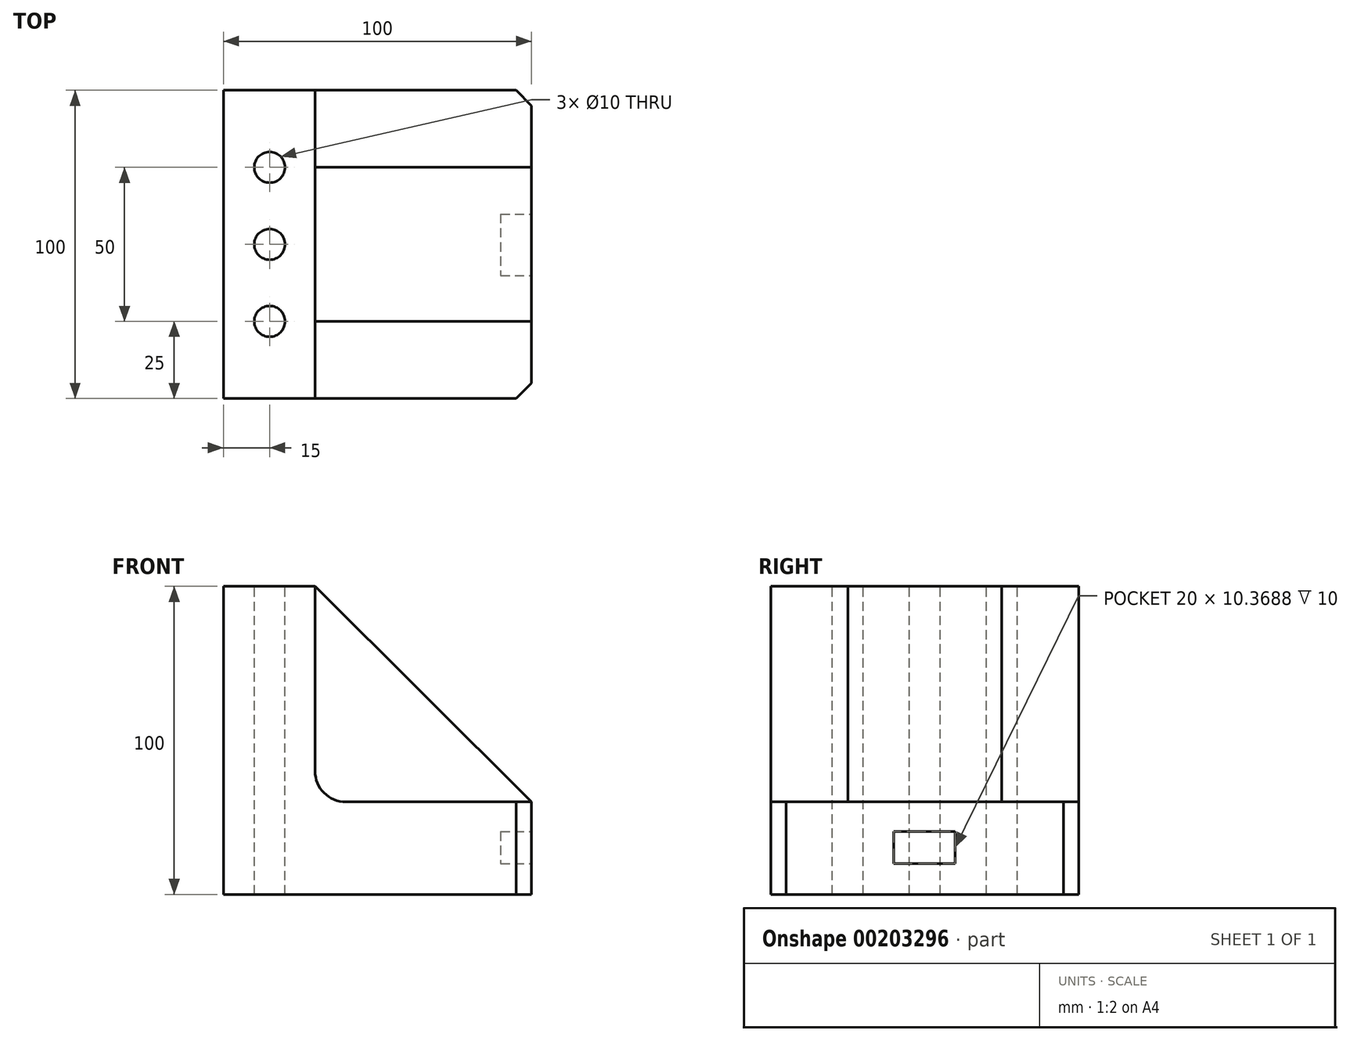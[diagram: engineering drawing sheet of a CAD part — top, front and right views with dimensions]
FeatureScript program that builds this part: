
annotation { "Feature Type Name" : "Feature", "Feature Type Description" : "" }
export const myFeature = defineFeature(function(context is Context, id is Id, definition is map)
    precondition{}
    {
        {
            var Q0;
            Q0=qCreatedBy(makeId("Top.planeOp"),FACE);
            var sketch = newSketch(context, id + "F0", { "sketchPlane" : qUnion([Q0])});
            skLineSegment(sketch, "E0.bottom", {"start": v(0, 0) * mm, "end": v(100, 0) * mm});
            skLineSegment(sketch, "E0.top", {"start": v(0, 100) * mm, "end": v(100, 100) * mm});
            skLineSegment(sketch, "E0.left", {"start": v(0, 0) * mm, "end": v(0, 100) * mm});
            skLineSegment(sketch, "E0.right", {"start": v(100, 0) * mm, "end": v(100, 100) * mm});
            skSolve(sketch);
        }
        {
            var Q0;
            Q0=makeQuery(id+"F0.imprint","IMPRINT",FACE,{"disambiguationData":[TD([[makeQuery(id+"F0.imprint","IMPRINT",EDGE,{"derivedFrom":sQuery(id+"F0.wireOp",EDGE,"E0.bottom")}),1.0]])]});
            extrude(context, id + "F1", {"entities" : qUnion([Q0]), "depth" : 100 * mm});
        }
        {
            var Q0;
            Q0=makeQuery(id+"F1.opExtrude","CAP_FACE",FACE,{"disambiguationData":[OSD([sQuery(id+"F0.wireOp",EDGE,"E0.bottom"),sQuery(id+"F0.wireOp",EDGE,"E0.top"),sQuery(id+"F0.wireOp",EDGE,"E0.left"),sQuery(id+"F0.wireOp",EDGE,"E0.right")])],"isStart":false});
            var sketch = newSketch(context, id + "F2", { "sketchPlane" : qUnion([Q0])});
            skLineSegment(sketch, "E1", {"start": v(0, 0) * mm, "end": v(30, 0) * mm});
            skLineSegment(sketch, "E2", {"start": v(30, 0) * mm, "end": v(30, 100) * mm});
            skCircle(sketch, "E3", {"center": v(15, 25) * mm, "radius": 5 * mm});
            skCircle(sketch, "E4", {"center": v(15, 50) * mm, "radius": 5 * mm});
            skCircle(sketch, "E5", {"center": v(15, 75) * mm, "radius": 5 * mm});
            skLineSegment(sketch, "E6", {"start": v(30, 0) * mm, "end": v(30, 25) * mm});
            skLineSegment(sketch, "E7", {"start": v(30, 100) * mm, "end": v(30, 75) * mm});
            skSolve(sketch);
        }
        {
            var Q0;
            Q0=makeQuery(id+"F2.imprint","IMPRINT",FACE,{"disambiguationData":[TD([[makeQuery(id+"F2.imprint","IMPRINT",EDGE,{"derivedFrom":sQuery(id+"F2.wireOp",EDGE,"E3")}),1.0]])]});
            var Q1;
            Q1=makeQuery(id+"F2.imprint","IMPRINT",FACE,{"disambiguationData":[TD([[makeQuery(id+"F2.imprint","IMPRINT",EDGE,{"derivedFrom":sQuery(id+"F2.wireOp",EDGE,"E4")}),1.0]])]});
            var Q2;
            Q2=makeQuery(id+"F2.imprint","IMPRINT",FACE,{"disambiguationData":[TD([[makeQuery(id+"F2.imprint","IMPRINT",EDGE,{"derivedFrom":sQuery(id+"F2.wireOp",EDGE,"E5")}),1.0]])]});
            extrude(context, id + "F3", {"entities" : qUnion([Q0, Q1, Q2]), "operationType" : NewBodyOperationType.REMOVE, "oppositeDirection" : true, "depth" : 100 * mm});
        }
        {
            var Q0;
            Q0=makeQuery(id+"F1.opExtrude","SWEPT_FACE",FACE,{"disambiguationData":[OSD([sQuery(id+"F0.wireOp",EDGE,"E0.bottom")])]});
            var sketch = newSketch(context, id + "F4", { "sketchPlane" : qUnion([Q0])});
            skLineSegment(sketch, "E8", {"start": v(50, 0) * mm, "end": v(50, 30) * mm});
            skPoint(sketch, "E9", {"position": v(29.74, 30) * mm});
            skLineSegment(sketch, "E10", {"start": v(29.74, 40) * mm, "end": v(29.74, 100) * mm});
            skArc(sketch, "E11.filletArc", {"start": v(29.74, 40) * mm, "mid": v(32.67, 32.93) * mm, "end": v(39.74, 30) * mm});
            skLineSegment(sketch, "E12", {"start": v(39.74, 30) * mm, "end": v(100, 30) * mm});
            skSolve(sketch);
        }
        {
            var Q0;
            Q0 = qSketchRegion(id + "F4", true);
            var Q1;
            {var subQ5=sQuery(id+"F4.wireOp",EDGE,"E10");Q1=makeQuery(id+"F4.imprint","IMPRINT",FACE,{"disambiguationData":[TD([[makeQuery(id+"F4.imprint","IMPRINT",EDGE,{"derivedFrom":subQ5}),-1.0]])]});}
            extrude(context, id + "F5", {"entities" : qUnion([Q0, Q1]), "operationType" : NewBodyOperationType.REMOVE, "oppositeDirection" : true, "depth" : 25 * mm});
        }
        {
            var Q0;
            Q0=makeQuery(id+"F1.opExtrude","SWEPT_FACE",FACE,{"disambiguationData":[OSD([sQuery(id+"F0.wireOp",EDGE,"E0.right")])]});
            var sketch = newSketch(context, id + "F6", { "sketchPlane" : qUnion([Q0])});
            skLineSegment(sketch, "E13", {"start": v(25, 30) * mm, "end": v(100, 30) * mm});
            skSolve(sketch);
        }
        {
            var Q0;
            Q0=makeQuery(id+"F1.opExtrude","SWEPT_FACE",FACE,{"disambiguationData":[OSD([sQuery(id+"F0.wireOp",EDGE,"E0.top")])]});
            var sketch = newSketch(context, id + "F7", { "sketchPlane" : qUnion([Q0])});
            skPoint(sketch, "E14", {"position": v(-29.74, 100) * mm});
            skPoint(sketch, "E15", {"position": v(-29.74, 30) * mm});
            skLineSegment(sketch, "E16", {"start": v(-39.74, 30) * mm, "end": v(-100, 30) * mm});
            skLineSegment(sketch, "E17", {"start": v(-29.74, 100) * mm, "end": v(-29.74, 40) * mm});
            skArc(sketch, "E18.filletArc", {"start": v(-39.74, 30) * mm, "mid": v(-32.67, 32.93) * mm, "end": v(-29.74, 40) * mm});
            skSolve(sketch);
        }
        {
            var Q0;
            {var subQ4=sQuery(id+"F7.wireOp",EDGE,"E16");Q0=makeQuery(id+"F7.imprint","IMPRINT",FACE,{"disambiguationData":[TD([[makeQuery(id+"F7.imprint","IMPRINT",EDGE,{"derivedFrom":subQ4}),-1.0]])]});}
            extrude(context, id + "F8", {"entities" : qUnion([Q0]), "operationType" : NewBodyOperationType.REMOVE, "oppositeDirection" : true, "depth" : 25 * mm});
        }
        {
            var Q0;
            Q0=makeQuery(id+"F5.boolean.opBoolean","COPY",FACE,{"derivedFrom":makeQuery(id+"F5.opExtrude","CAP_FACE",FACE,{"disambiguationData":[OSD([sQuery(id+"F0.wireOp",EDGE,"E0.bottom"),sQuery(id+"F0.wireOp",EDGE,"E0.right"),sQuery(id+"F4.wireOp",EDGE,"E10"),sQuery(id+"F4.wireOp",EDGE,"E11.filletArc"),sQuery(id+"F4.wireOp",EDGE,"E12")])],"isStart":false})});
            var sketch = newSketch(context, id + "F9", { "sketchPlane" : qUnion([Q0])});
            skLineSegment(sketch, "E19", {"start": v(29.74, 100) * mm, "end": v(100, 30) * mm});
            skSolve(sketch);
        }
        {
            var Q0;
            Q0=makeQuery(id+"F9.imprint","IMPRINT",FACE,{"disambiguationData":[TD([[makeQuery(id+"F9.imprint","IMPRINT",EDGE,{"derivedFrom":sQuery(id+"F9.wireOp",EDGE,"E19")}),1.0]])]});
            extrude(context, id + "F10", {"entities" : qUnion([Q0]), "operationType" : NewBodyOperationType.REMOVE, "oppositeDirection" : true, "depth" : 25 * mm});
        }
        {
            var Q0;
            Q0=makeQuery(id+"F10.boolean.opBoolean","COPY",FACE,{"derivedFrom":makeQuery(id+"F10.opExtrude","CAP_FACE",FACE,{"disambiguationData":[OSD([sQuery(id+"F0.wireOp",EDGE,"E0.bottom"),sQuery(id+"F0.wireOp",EDGE,"E0.right"),sQuery(id+"F9.wireOp",EDGE,"E19")])],"isStart":false})});
            extrude(context, id + "F11", {"entities" : qUnion([Q0]), "operationType" : NewBodyOperationType.REMOVE, "oppositeDirection" : true, "depth" : 25 * mm});
        }
        {
            var Q0;
            Q0=makeQuery(id+"F1.opExtrude","SWEPT_EDGE",EDGE,{"disambiguationData":[OSD([sQuery(id+"F0.wireOp",EDGE,"E0.bottom"),sQuery(id+"F0.wireOp",EDGE,"E0.right")])]});
            var Q1;
            Q1=makeQuery(id+"F1.opExtrude","SWEPT_EDGE",EDGE,{"disambiguationData":[OSD([sQuery(id+"F0.wireOp",EDGE,"E0.top"),sQuery(id+"F0.wireOp",EDGE,"E0.right")])]});
            chamfer(context, id + "F12", {"entities" : qUnion([Q0, Q1]), "width" : 5 * mm, "tangentPropagation" : true});
        }
        {
            var Q0;
            {var subQ3=sQuery(id+"F6.wireOp",EDGE,"E13");Q0=makeQuery(id+"F6.imprint","IMPRINT",FACE,{"disambiguationData":[TD([[makeQuery(id+"F6.imprint","IMPRINT",EDGE,{"derivedFrom":subQ3}),-1.0]])]});}
            var sketch = newSketch(context, id + "F13", { "sketchPlane" : qUnion([Q0])});
            skPoint(sketch, "E20", {"position": v(24.79, 30.4) * mm});
            skPoint(sketch, "E21", {"position": v(74.95, 30.31) * mm});
            skLineSegment(sketch, "E22", {"start": v(24.79, 30.4) * mm, "end": v(74.95, 30.31) * mm});
            skLineSegment(sketch, "E23", {"start": v(49.87, 10) * mm, "end": v(59.87, 10) * mm});
            skPoint(sketch, "E24", {"position": v(59.87, 10) * mm});
            skLineSegment(sketch, "E25", {"start": v(49.87, 10) * mm, "end": v(39.87, 10) * mm});
            skPoint(sketch, "E26", {"position": v(39.87, 10) * mm});
            skLineSegment(sketch, "E27.bottom", {"start": v(39.87, 20.37) * mm, "end": v(59.87, 20.37) * mm});
            skLineSegment(sketch, "E27.top", {"start": v(39.87, 10) * mm, "end": v(59.87, 10) * mm});
            skLineSegment(sketch, "E27.left", {"start": v(39.87, 20.37) * mm, "end": v(39.87, 10) * mm});
            skLineSegment(sketch, "E27.right", {"start": v(59.87, 20.37) * mm, "end": v(59.87, 10) * mm});
            skSolve(sketch);
        }
        {
            var Q0;
            Q0=makeQuery(id+"F13.imprint","IMPRINT",FACE,{"disambiguationData":[TD([[makeQuery(id+"F13.imprint","IMPRINT",EDGE,{"derivedFrom":sQuery(id+"F13.wireOp",EDGE,"E27.bottom")}),-1.0]])]});
            extrude(context, id + "F14", {"entities" : qUnion([Q0]), "operationType" : NewBodyOperationType.REMOVE, "oppositeDirection" : true, "depth" : 10 * mm});
        }
    });
